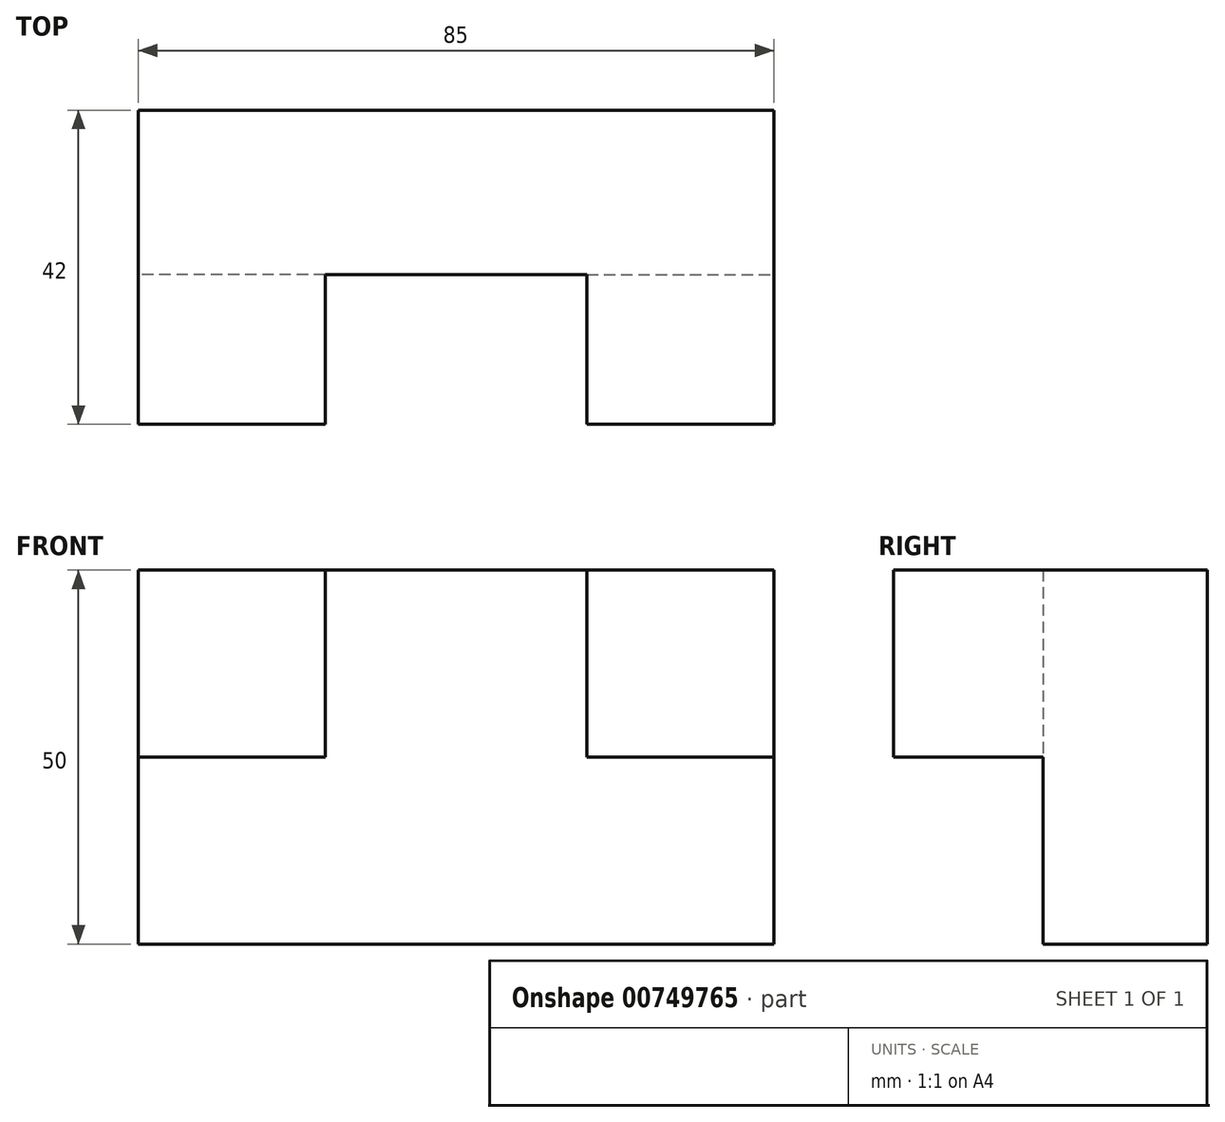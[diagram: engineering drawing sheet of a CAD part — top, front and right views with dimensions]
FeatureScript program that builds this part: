
annotation { "Feature Type Name" : "Feature", "Feature Type Description" : "" }
export const myFeature = defineFeature(function(context is Context, id is Id, definition is map)
    precondition{}
    {
        {
            var Q0;
            Q0=qCreatedBy(makeId("Front.planeOp"),FACE);
            var sketch = newSketch(context, id + "F0", { "sketchPlane" : qUnion([Q0])});
            skLineSegment(sketch, "E0", {"start": v(0, 0) * mm, "end": v(0, 50) * mm});
            skLineSegment(sketch, "E1", {"start": v(0, 50) * mm, "end": v(85, 50) * mm});
            skLineSegment(sketch, "E2", {"start": v(85, 50) * mm, "end": v(85, 0) * mm});
            skLineSegment(sketch, "E3", {"start": v(85, 0) * mm, "end": v(0, 0) * mm});
            skSolve(sketch);
        }
        {
            var Q0;
            Q0=makeQuery(id+"F0.imprint","IMPRINT",FACE,{"disambiguationData":[TD([[makeQuery(id+"F0.imprint","IMPRINT",EDGE,{"derivedFrom":sQuery(id+"F0.wireOp",EDGE,"E0")}),-1.0]])]});
            extrude(context, id + "F1", {"entities" : qUnion([Q0]), "depth" : 22 * mm, "offsetDistance" : 25 * mm});
        }
        {
            var Q0;
            Q0=makeQuery(id+"F1.opExtrude","CAP_FACE",FACE,{"disambiguationData":[OSD([sQuery(id+"F0.wireOp",EDGE,"E0"),sQuery(id+"F0.wireOp",EDGE,"E1"),sQuery(id+"F0.wireOp",EDGE,"E2"),sQuery(id+"F0.wireOp",EDGE,"E3")])],"isStart":false});
            var sketch = newSketch(context, id + "F2", { "sketchPlane" : qUnion([Q0])});
            skLineSegment(sketch, "E4", {"start": v(0, 50) * mm, "end": v(25, 50) * mm});
            skLineSegment(sketch, "E5", {"start": v(25, 50) * mm, "end": v(25, 25) * mm});
            skLineSegment(sketch, "E6", {"start": v(25, 25) * mm, "end": v(0, 25) * mm});
            skLineSegment(sketch, "E7", {"start": v(0, 25) * mm, "end": v(0, 50) * mm});
            skLineSegment(sketch, "E8", {"start": v(85, 50) * mm, "end": v(60, 50) * mm});
            skLineSegment(sketch, "E9", {"start": v(60, 50) * mm, "end": v(60, 25) * mm});
            skLineSegment(sketch, "E10", {"start": v(60, 25) * mm, "end": v(85, 25) * mm});
            skLineSegment(sketch, "E11", {"start": v(85, 25) * mm, "end": v(85, 50) * mm});
            skSolve(sketch);
        }
        {
            var Q0;
            Q0=makeQuery(id+"F2.imprint","IMPRINT",FACE,{"disambiguationData":[TD([[makeQuery(id+"F2.imprint","IMPRINT",EDGE,{"derivedFrom":sQuery(id+"F2.wireOp",EDGE,"E4")}),-1.0]])]});
            extrude(context, id + "F3", {"entities" : qUnion([Q0]), "operationType" : NewBodyOperationType.ADD, "depth" : 20 * mm, "offsetDistance" : 25 * mm});
        }
        {
            var Q0;
            Q0 = qSketchRegion(id + "F2", true);
            extrude(context, id + "F4", {"entities" : qUnion([Q0]), "operationType" : NewBodyOperationType.ADD, "depth" : 20 * mm, "offsetDistance" : 25 * mm});
        }
    });
